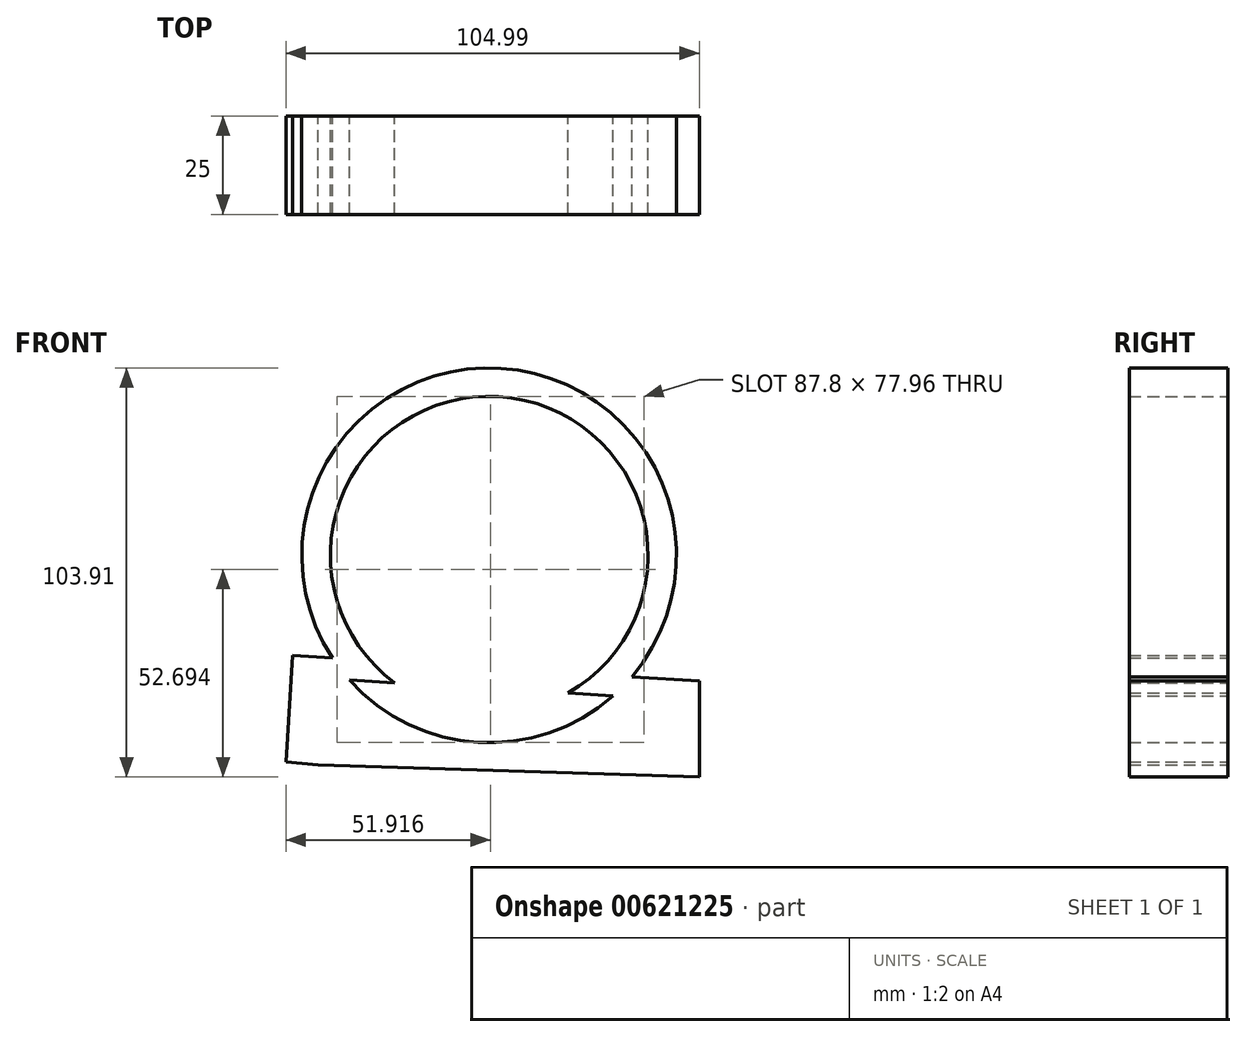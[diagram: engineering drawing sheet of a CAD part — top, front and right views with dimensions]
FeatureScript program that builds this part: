
annotation { "Feature Type Name" : "Feature", "Feature Type Description" : "" }
export const myFeature = defineFeature(function(context is Context, id is Id, definition is map)
    precondition{}
    {
        {
            var Q0;
            Q0=qCreatedBy(makeId("Front.planeOp"),FACE);
            var sketch = newSketch(context, id + "F0", { "sketchPlane" : qUnion([Q0])});
            skCircle(sketch, "E0", {"center": v(0, 0) * mm, "radius": 47.6 * mm});
            skCircle(sketch, "E1", {"center": v(0, 0) * mm, "radius": 40.36 * mm});
            skLineSegment(sketch, "E2", {"start": v(-43.04, -31.23) * mm, "end": v(46.32, -36.62) * mm});
            skLineSegment(sketch, "E3", {"start": v(46.32, -36.62) * mm, "end": v(46.32, -51.79) * mm});
            skLineSegment(sketch, "E4", {"start": v(46.32, -51.79) * mm, "end": v(-43.52, -46.4) * mm});
            skLineSegment(sketch, "E5", {"start": v(-43.52, -46.4) * mm, "end": v(-43.04, -31.23) * mm});
            skLineSegment(sketch, "E6", {"start": v(-43.52, -53.24) * mm, "end": v(53.4, -56.31) * mm});
            skLineSegment(sketch, "E7", {"start": v(53.4, -56.31) * mm, "end": v(53.4, -31.94) * mm});
            skLineSegment(sketch, "E8", {"start": v(53.4, -31.94) * mm, "end": v(-49.89, -25.4) * mm});
            skLineSegment(sketch, "E9", {"start": v(-49.89, -25.4) * mm, "end": v(-51.6, -52.48) * mm});
            skLineSegment(sketch, "E10", {"start": v(-51.6, -52.48) * mm, "end": v(-43.52, -53.24) * mm});
            skSolve(sketch);
        }
        {
            var Q0;
            Q0 = qSketchRegion(id + "F0", true);
            var Q1;
            {var subQ0=sQuery(id+"F0.wireOp",EDGE,"E3");Q1=makeQuery(id+"F0.imprint","IMPRINT",FACE,{"disambiguationData":[TD([[makeQuery(id+"F0.imprint","IMPRINT",EDGE,{"derivedFrom":subQ0}),-1.0]])]});}
            extrude(context, id + "F1", {"entities" : qUnion([Q0, Q1]), "depth" : 25 * mm, "offsetDistance" : 25 * mm});
        }
    });
